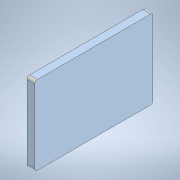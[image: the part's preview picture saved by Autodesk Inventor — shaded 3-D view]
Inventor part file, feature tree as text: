
AUTODESK INVENTOR PART (.ipt)
format: ipt  version: 2022 (Build 260153070, 153G)  size: 100,352 bytes
history: native  units: in
note: dims shown in document units (in); Inventor stores cm internally (conversion verified against a paired STEP export)
features: extrude x1, fillet x1, sketch x1
ambient origin geometry x8: Origin, YZ Plane, XZ Plane, XY Plane, X Axis, Y Axis, Z Axis, Center Point
bodies: Solid1 (feature_tree)
feature tree (3):
  extrude  "Extrusion1"  Depth=4.0in
  fillet  "Fillet1"  Radius=0.4in
  sketch  "Sketch1"  dims[d0=6.0in d1=4.0in d2=0.4in d3=0.0in d4=0.125in]
